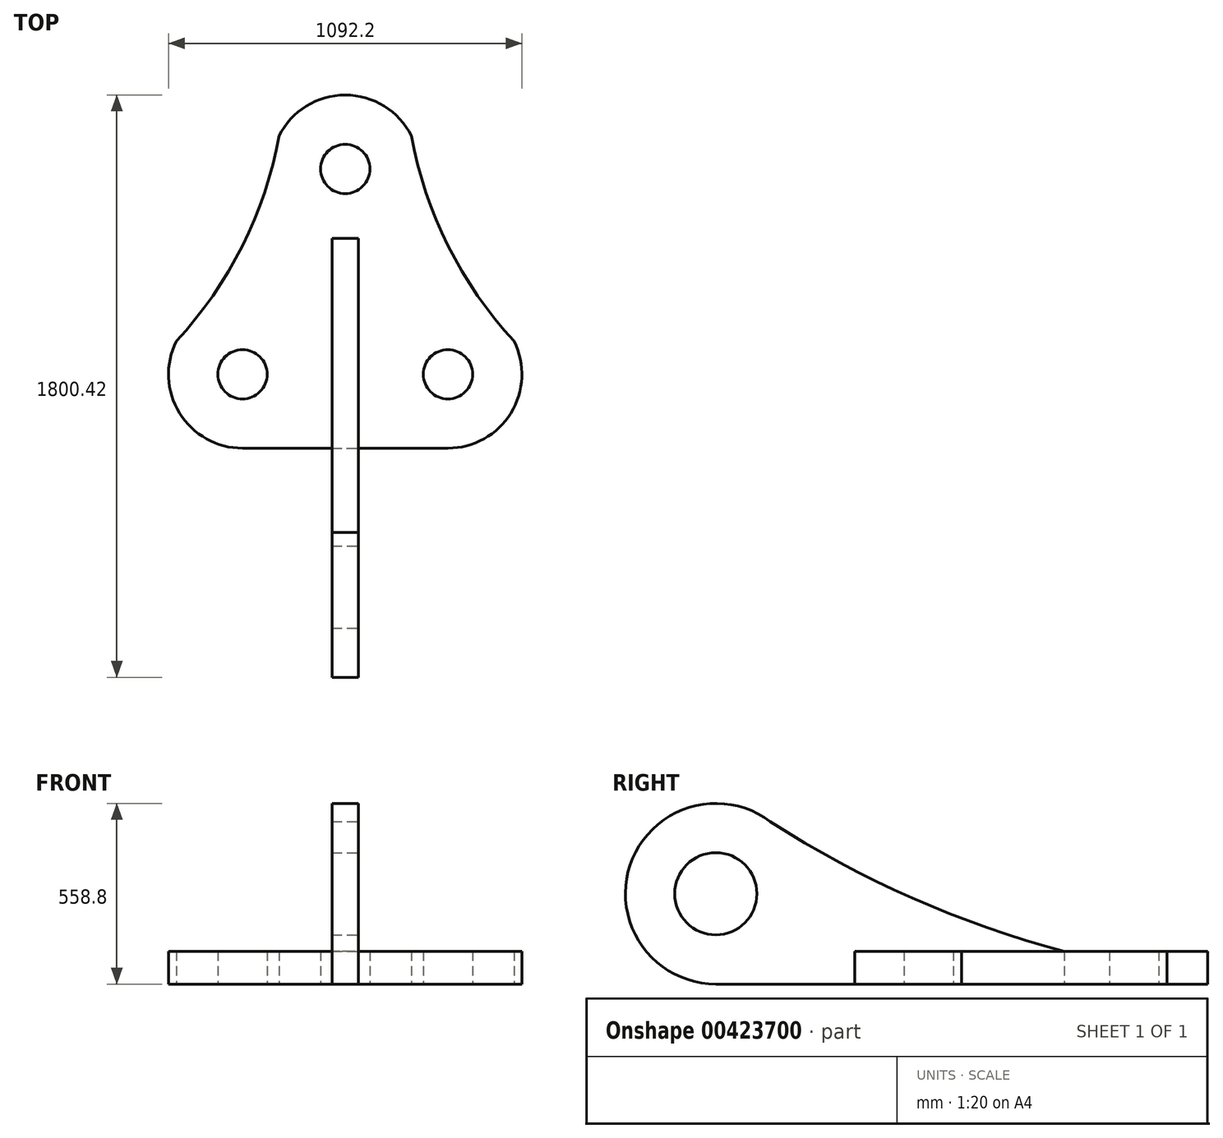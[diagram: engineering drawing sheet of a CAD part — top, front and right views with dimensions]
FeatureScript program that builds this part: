
annotation { "Feature Type Name" : "Feature", "Feature Type Description" : "" }
export const myFeature = defineFeature(function(context is Context, id is Id, definition is map)
    precondition{}
    {
        {
            var Q0;
            Q0=qCreatedBy(makeId("Top.planeOp"),FACE);
            var sketch = newSketch(context, id + "F0", { "sketchPlane" : qUnion([Q0])});
            skCircle(sketch, "E0", {"center": v(-317.5, -579.14) * mm, "radius": 76.2 * mm});
            skCircle(sketch, "E1", {"center": v(317.5, -579.14) * mm, "radius": 76.2 * mm});
            skCircle(sketch, "E2", {"center": v(0, 55.86) * mm, "radius": 76.2 * mm});
            skArc(sketch, "E3", {"start": v(204.47, 158.1) * mm, "mid": v(0, 284.46) * mm, "end": v(-204.47, 158.1) * mm});
            skArc(sketch, "E4", {"start": v(-521.97, -476.9) * mm, "mid": v(-511.96, -699.32) * mm, "end": v(-317.5, -807.74) * mm});
            skArc(sketch, "E5", {"start": v(317.5, -807.74) * mm, "mid": v(511.96, -699.32) * mm, "end": v(521.97, -476.9) * mm});
            skArc(sketch, "E6", {"start": v(204.47, 158.1) * mm, "mid": v(317.94, -182.04) * mm, "end": v(521.97, -476.9) * mm});
            skArc(sketch, "E7", {"start": v(-521.97, -476.9) * mm, "mid": v(-317.94, -182.04) * mm, "end": v(-204.47, 158.1) * mm});
            skLineSegment(sketch, "E8", {"start": v(-317.5, -807.74) * mm, "end": v(317.5, -807.74) * mm});
            skSolve(sketch);
        }
        {
            var Q0;
            Q0 = qSketchRegion(id + "F0", true);
            extrude(context, id + "F1", {"entities" : qUnion([Q0]), "depth" : 101.6 * mm});
        }
        {
            var Q0;
            Q0=qCreatedBy(makeId("Right.planeOp"),FACE);
            var sketch = newSketch(context, id + "F2", { "sketchPlane" : qUnion([Q0])});
            skLineSegment(sketch, "E9", {"start": v(71.04, 0) * mm, "end": v(-1236.56, 0) * mm});
            skCircle(sketch, "E10", {"center": v(-1236.56, 279.4) * mm, "radius": 279.4 * mm});
            skCircle(sketch, "E11", {"center": v(-1236.56, 279.4) * mm, "radius": 127 * mm});
            skArc(sketch, "E12", {"start": v(-1100.12, 523.22) * mm, "mid": v(-646.99, 273.98) * mm, "end": v(-159.4, 101.6) * mm});
            skLineSegment(sketch, "E13", {"start": v(-159.4, 101.6) * mm, "end": v(-159.4, 0) * mm});
            skSolve(sketch);
        }
        {
            var Q0;
            Q0 = qSketchRegion(id + "F2", true);
            extrude(context, id + "F3", {"entities" : qUnion([Q0]), "endBound" : BoundingType.SYMMETRIC, "oppositeDirection" : true, "depth" : 81.28 * mm});
        }
    });
